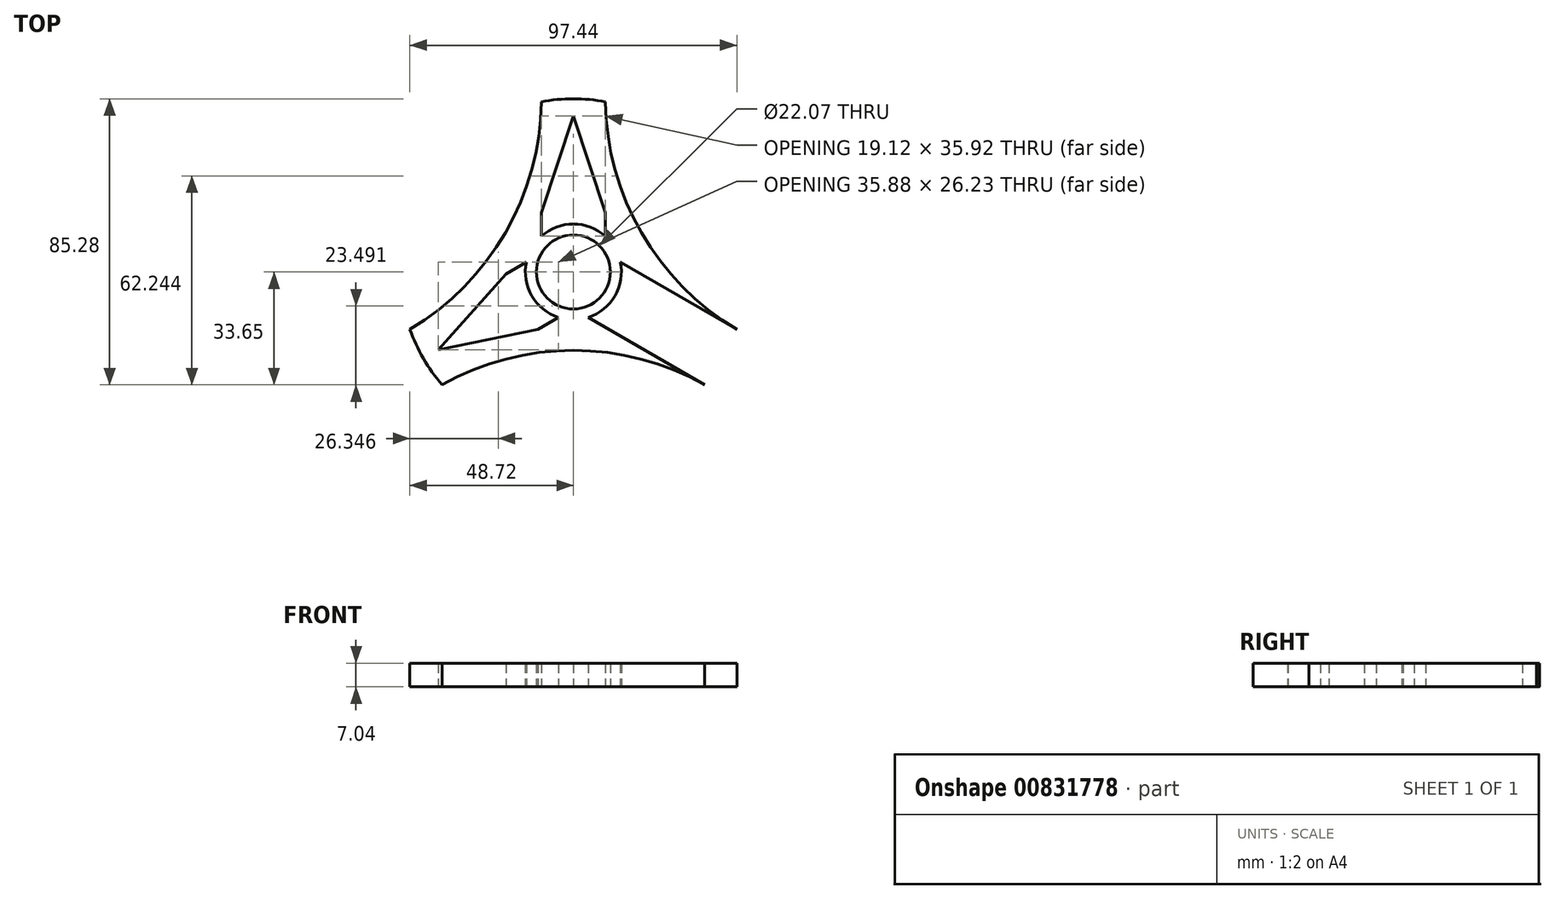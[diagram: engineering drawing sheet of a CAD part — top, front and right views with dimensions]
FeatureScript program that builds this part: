
annotation { "Feature Type Name" : "Feature", "Feature Type Description" : "" }
export const myFeature = defineFeature(function(context is Context, id is Id, definition is map)
    precondition{}
    {
        {
            var Q0;
            Q0=qCreatedBy(makeId("Top.planeOp"),FACE);
            var sketch = newSketch(context, id + "F0", { "sketchPlane" : qUnion([Q0])});
            skCircle(sketch, "E0", {"center": v(0, 0) * mm, "radius": 11.04 * mm});
            skLineSegment(sketch, "E1", {"start": v(0, 0) * mm, "end": v(0, 11.04) * mm});
            skLineSegment(sketch, "E2", {"start": v(0, 0) * mm, "end": v(9.56, -5.52) * mm});
            skLineSegment(sketch, "E3", {"start": v(0, 0) * mm, "end": v(-9.56, -5.52) * mm});
            skLineSegment(sketch, "E4.bottom", {"start": v(-9.56, -5.52) * mm, "end": v(9.56, -5.52) * mm});
            skLineSegment(sketch, "E4.top", {"start": v(-9.56, 51.63) * mm, "end": v(9.56, 51.63) * mm});
            skLineSegment(sketch, "E4.left", {"start": v(-9.56, -5.52) * mm, "end": v(-9.56, 51.63) * mm});
            skLineSegment(sketch, "E4.right", {"start": v(9.56, -5.52) * mm, "end": v(9.56, 51.63) * mm});
            skLineSegment(sketch, "E5", {"start": v(0, 11.04) * mm, "end": v(49.5, -17.54) * mm});
            skLineSegment(sketch, "E6", {"start": v(-9.56, -5.52) * mm, "end": v(39.94, -34.1) * mm});
            skLineSegment(sketch, "E7", {"start": v(39.94, -34.1) * mm, "end": v(49.5, -17.54) * mm});
            skLineSegment(sketch, "E8", {"start": v(9.56, -5.52) * mm, "end": v(-39.94, -34.1) * mm});
            skLineSegment(sketch, "E9", {"start": v(0, 11.04) * mm, "end": v(-49.5, -17.54) * mm});
            skLineSegment(sketch, "E10", {"start": v(-49.5, -17.54) * mm, "end": v(-39.94, -34.1) * mm});
            skArc(sketch, "E11", {"start": v(39.94, -34.1) * mm, "mid": v(0, -23.4) * mm, "end": v(-39.94, -34.1) * mm});
            skArc(sketch, "E12", {"start": v(9.56, 51.63) * mm, "mid": v(20.26, 11.7) * mm, "end": v(49.5, -17.54) * mm});
            skArc(sketch, "E13", {"start": v(-49.5, -17.54) * mm, "mid": v(-20.26, 11.7) * mm, "end": v(-9.56, 51.63) * mm});
            skCircle(sketch, "E14", {"center": v(0, 0) * mm, "radius": 14.3 * mm});
            skLineSegment(sketch, "E15", {"start": v(0, 51.63) * mm, "end": v(0, 46.55) * mm});
            skLineSegment(sketch, "E16", {"start": v(9.56, 51.63) * mm, "end": v(4.48, 51.63) * mm});
            skPoint(sketch, "E17", {"position": v(-4.48, 51.63) * mm});
            skLineSegment(sketch, "E18", {"start": v(-4.48, 51.63) * mm, "end": v(-9.56, 51.63) * mm});
            skLineSegment(sketch, "E19", {"start": v(0, 46.55) * mm, "end": v(5.08, 46.55) * mm});
            skLineSegment(sketch, "E20", {"start": v(5.08, 46.55) * mm, "end": v(-5.08, 46.55) * mm});
            skLineSegment(sketch, "E21", {"start": v(49.5, -17.54) * mm, "end": v(45.1, -15) * mm});
            skLineSegment(sketch, "E22", {"start": v(39.94, -34.1) * mm, "end": v(35.54, -31.55) * mm});
            skLineSegment(sketch, "E23", {"start": v(45.1, -15) * mm, "end": v(35.54, -31.55) * mm});
            skLineSegment(sketch, "E24", {"start": v(35.54, -31.55) * mm, "end": v(37.74, -27.74) * mm});
            skPoint(sketch, "E24.endSnap0", {"position": v(37.74, -32.82) * mm});
            skLineSegment(sketch, "E25", {"start": v(45.1, -15) * mm, "end": v(42.55, -19.4) * mm});
            skCircle(sketch, "E26", {"center": v(0, 0) * mm, "radius": 20.13 * mm});
            skPoint(sketch, "E27", {"position": v(-9.56, 17.71) * mm});
            skPoint(sketch, "E28", {"position": v(9.56, 17.71) * mm});
            skPoint(sketch, "E29", {"position": v(20.12, -0.58) * mm});
            skPoint(sketch, "E30", {"position": v(10.56, -17.13) * mm});
            skPoint(sketch, "E31", {"position": v(-10.56, -17.13) * mm});
            skPoint(sketch, "E32", {"position": v(-20.12, -0.58) * mm});
            skLineSegment(sketch, "E33", {"start": v(9.56, 17.71) * mm, "end": v(0, 46.55) * mm});
            skLineSegment(sketch, "E34", {"start": v(-9.56, 17.71) * mm, "end": v(0, 46.55) * mm});
            skLineSegment(sketch, "E35", {"start": v(40.32, -23.28) * mm, "end": v(20.12, -0.58) * mm});
            skLineSegment(sketch, "E36", {"start": v(10.56, -17.13) * mm, "end": v(40.32, -23.28) * mm});
            skLineSegment(sketch, "E37", {"start": v(9.56, -5.52) * mm, "end": v(0, 11.04) * mm});
            skPoint(sketch, "E38", {"position": v(-44.71, -25.82) * mm});
            skLineSegment(sketch, "E39", {"start": v(-44.71, -25.82) * mm, "end": v(-28.62, -16.52) * mm});
            skPoint(sketch, "E40", {"position": v(-36.67, -21.17) * mm});
            skPoint(sketch, "E41", {"position": v(-40.32, -23.28) * mm});
            skLineSegment(sketch, "E42", {"start": v(-40.32, -23.28) * mm, "end": v(-10.56, -17.13) * mm});
            skLineSegment(sketch, "E43", {"start": v(-40.32, -23.28) * mm, "end": v(-20.12, -0.58) * mm});
            skCircle(sketch, "E44", {"center": v(0, 0) * mm, "radius": 51.63 * mm});
            skSolve(sketch);
        }
        {
            var Q0;
            {var subQ4=sQuery(id+"F0.wireOp",EDGE,"E15");Q0=makeQuery(id+"F0.imprint","IMPRINT",FACE,{"disambiguationData":[TD([[makeQuery(id+"F0.imprint","IMPRINT",EDGE,{"derivedFrom":subQ4}),-1.0]])]});}
            var Q1;
            {var subQ4=sQuery(id+"F0.wireOp",EDGE,"E15");Q1=makeQuery(id+"F0.imprint","IMPRINT",FACE,{"disambiguationData":[TD([[makeQuery(id+"F0.imprint","IMPRINT",EDGE,{"derivedFrom":subQ4}),1.0]])]});}
            var Q2;
            {var subQ1=sQuery(id+"F0.wireOp",EDGE,"E4.right");var subQ3=sQuery(id+"F0.wireOp",EDGE,"E14");var subQ4=makeQuery(id+"F0.imprint","INTERSECT",VERTEX,{"derivedFrom":[subQ1,subQ3]});Q2=makeQuery(id+"F0.imprint","IMPRINT",FACE,{"disambiguationData":[TD([[makeQuery(id+"F0.imprint","IMPRINT",EDGE,{"disambiguationData":[TD([[subQ4,1.0]])],"derivedFrom":subQ3}),-1.0]])]});}
            var Q3;
            {var subQ1=sQuery(id+"F0.wireOp",EDGE,"E6");var subQ3=sQuery(id+"F0.wireOp",EDGE,"E14");var subQ4=makeQuery(id+"F0.imprint","INTERSECT",VERTEX,{"derivedFrom":[subQ1,subQ3]});Q3=makeQuery(id+"F0.imprint","IMPRINT",FACE,{"disambiguationData":[TD([[makeQuery(id+"F0.imprint","IMPRINT",EDGE,{"disambiguationData":[TD([[subQ4,1.0]])],"derivedFrom":subQ3}),-1.0]])]});}
            var Q4;
            {var subQ1=sQuery(id+"F0.wireOp",EDGE,"E4.left");var subQ3=sQuery(id+"F0.wireOp",EDGE,"E14");var subQ4=makeQuery(id+"F0.imprint","INTERSECT",VERTEX,{"derivedFrom":[subQ1,subQ3]});Q4=makeQuery(id+"F0.imprint","IMPRINT",FACE,{"disambiguationData":[TD([[makeQuery(id+"F0.imprint","IMPRINT",EDGE,{"disambiguationData":[TD([[subQ4,-1.0]])],"derivedFrom":subQ3}),-1.0]])]});}
            var Q5;
            {var subQ5=sQuery(id+"F0.wireOp",EDGE,"E44");var subQ6=sQuery(id+"F0.wireOp",EDGE,"E13");var subQ7=makeQuery(id+"F0.imprint","INTERSECT",VERTEX,{"disambiguationData":[OD(0.0)],"derivedFrom":[subQ6,subQ5]});Q5=makeQuery(id+"F0.imprint","IMPRINT",FACE,{"disambiguationData":[TD([[makeQuery(id+"F0.imprint","IMPRINT",EDGE,{"disambiguationData":[TD([[subQ7,-1.0]])],"derivedFrom":subQ6}),-1.0]])]});}
            var Q6;
            {var subQ3=sQuery(id+"F0.wireOp",EDGE,"E44");var subQ5=sQuery(id+"F0.wireOp",EDGE,"E12");var subQ6=makeQuery(id+"F0.imprint","INTERSECT",VERTEX,{"disambiguationData":[OD(0.0)],"derivedFrom":[subQ5,subQ3]});Q6=makeQuery(id+"F0.imprint","IMPRINT",FACE,{"disambiguationData":[TD([[makeQuery(id+"F0.imprint","IMPRINT",EDGE,{"disambiguationData":[TD([[subQ6,-1.0]])],"derivedFrom":subQ5}),-1.0]])]});}
            var Q7;
            {var subQ3=sQuery(id+"F0.wireOp",EDGE,"E44");var subQ5=sQuery(id+"F0.wireOp",EDGE,"E11");var subQ6=makeQuery(id+"F0.imprint","INTERSECT",VERTEX,{"disambiguationData":[OD(0.0)],"derivedFrom":[subQ5,subQ3]});Q7=makeQuery(id+"F0.imprint","IMPRINT",FACE,{"disambiguationData":[TD([[makeQuery(id+"F0.imprint","IMPRINT",EDGE,{"disambiguationData":[TD([[subQ6,-1.0]])],"derivedFrom":subQ5}),-1.0]])]});}
            var Q8;
            {var subQ0=sQuery(id+"F0.wireOp",EDGE,"E42");Q8=makeQuery(id+"F0.imprint","IMPRINT",FACE,{"disambiguationData":[TD([[makeQuery(id+"F0.imprint","IMPRINT",EDGE,{"derivedFrom":subQ0}),-1.0]])]});}
            var Q9;
            {var subQ0=sQuery(id+"F0.wireOp",EDGE,"E43");Q9=makeQuery(id+"F0.imprint","IMPRINT",FACE,{"disambiguationData":[TD([[makeQuery(id+"F0.imprint","IMPRINT",EDGE,{"derivedFrom":subQ0}),1.0]])]});}
            var Q10;
            {var subQ0=sQuery(id+"F0.wireOp",EDGE,"E24");Q10=makeQuery(id+"F0.imprint","IMPRINT",FACE,{"disambiguationData":[TD([[makeQuery(id+"F0.imprint","IMPRINT",EDGE,{"derivedFrom":subQ0}),1.0]])]});}
            var Q11;
            {var subQ0=sQuery(id+"F0.wireOp",EDGE,"E25");Q11=makeQuery(id+"F0.imprint","IMPRINT",FACE,{"disambiguationData":[TD([[makeQuery(id+"F0.imprint","IMPRINT",EDGE,{"derivedFrom":subQ0}),-1.0]])]});}
            var Q12;
            {var subQ0=sQuery(id+"F0.wireOp",EDGE,"E14");var subQ6=sQuery(id+"F0.wireOp",EDGE,"E8");var subQ7=makeQuery(id+"F0.imprint","INTERSECT",VERTEX,{"derivedFrom":[subQ6,subQ0]});Q12=makeQuery(id+"F0.imprint","IMPRINT",FACE,{"disambiguationData":[TD([[makeQuery(id+"F0.imprint","IMPRINT",EDGE,{"disambiguationData":[TD([[subQ7,1.0]])],"derivedFrom":subQ0}),1.0]])]});}
            var Q13;
            {var subQ0=sQuery(id+"F0.wireOp",EDGE,"E14");var subQ1=sQuery(id+"F0.wireOp",EDGE,"E4.left");var subQ2=makeQuery(id+"F0.imprint","INTERSECT",VERTEX,{"derivedFrom":[subQ1,subQ0]});Q13=makeQuery(id+"F0.imprint","IMPRINT",FACE,{"disambiguationData":[TD([[makeQuery(id+"F0.imprint","IMPRINT",EDGE,{"disambiguationData":[TD([[subQ2,-1.0]])],"derivedFrom":subQ0}),1.0]])]});}
            var Q14;
            {var subQ0=sQuery(id+"F0.wireOp",EDGE,"E14");var subQ6=sQuery(id+"F0.wireOp",EDGE,"E4.left");var subQ7=makeQuery(id+"F0.imprint","INTERSECT",VERTEX,{"derivedFrom":[subQ6,subQ0]});Q14=makeQuery(id+"F0.imprint","IMPRINT",FACE,{"disambiguationData":[TD([[makeQuery(id+"F0.imprint","IMPRINT",EDGE,{"disambiguationData":[TD([[subQ7,1.0]])],"derivedFrom":subQ0}),1.0]])]});}
            var Q15;
            {var subQ0=sQuery(id+"F0.wireOp",EDGE,"E14");var subQ1=sQuery(id+"F0.wireOp",EDGE,"E4.right");var subQ2=makeQuery(id+"F0.imprint","INTERSECT",VERTEX,{"derivedFrom":[subQ1,subQ0]});Q15=makeQuery(id+"F0.imprint","IMPRINT",FACE,{"disambiguationData":[TD([[makeQuery(id+"F0.imprint","IMPRINT",EDGE,{"disambiguationData":[TD([[subQ2,1.0]])],"derivedFrom":subQ0}),1.0]])]});}
            var Q16;
            {var subQ0=sQuery(id+"F0.wireOp",EDGE,"E14");var subQ8=sQuery(id+"F0.wireOp",EDGE,"E5");var subQ10=makeQuery(id+"F0.imprint","INTERSECT",VERTEX,{"derivedFrom":[subQ8,subQ0]});Q16=makeQuery(id+"F0.imprint","IMPRINT",FACE,{"disambiguationData":[TD([[makeQuery(id+"F0.imprint","IMPRINT",EDGE,{"disambiguationData":[TD([[subQ10,1.0]])],"derivedFrom":subQ0}),1.0]])]});}
            var Q17;
            {var subQ0=sQuery(id+"F0.wireOp",EDGE,"E14");var subQ1=sQuery(id+"F0.wireOp",EDGE,"E6");var subQ2=makeQuery(id+"F0.imprint","INTERSECT",VERTEX,{"derivedFrom":[subQ1,subQ0]});Q17=makeQuery(id+"F0.imprint","IMPRINT",FACE,{"disambiguationData":[TD([[makeQuery(id+"F0.imprint","IMPRINT",EDGE,{"disambiguationData":[TD([[subQ2,1.0]])],"derivedFrom":subQ0}),1.0]])]});}
            var Q18;
            {var subQ0=sQuery(id+"F0.wireOp",EDGE,"E24");Q18=makeQuery(id+"F0.imprint","IMPRINT",FACE,{"disambiguationData":[TD([[makeQuery(id+"F0.imprint","IMPRINT",EDGE,{"derivedFrom":subQ0}),-1.0]])]});}
            extrude(context, id + "F1", {"entities" : qUnion([Q0, Q1, Q2, Q3, Q4, Q5, Q6, Q7, Q8, Q9, Q10, Q11, Q12, Q13, Q14, Q15, Q16, Q17, Q18]), "depth" : 7.04 * mm, "offsetDistance" : 25.4 * mm});
        }
    });
